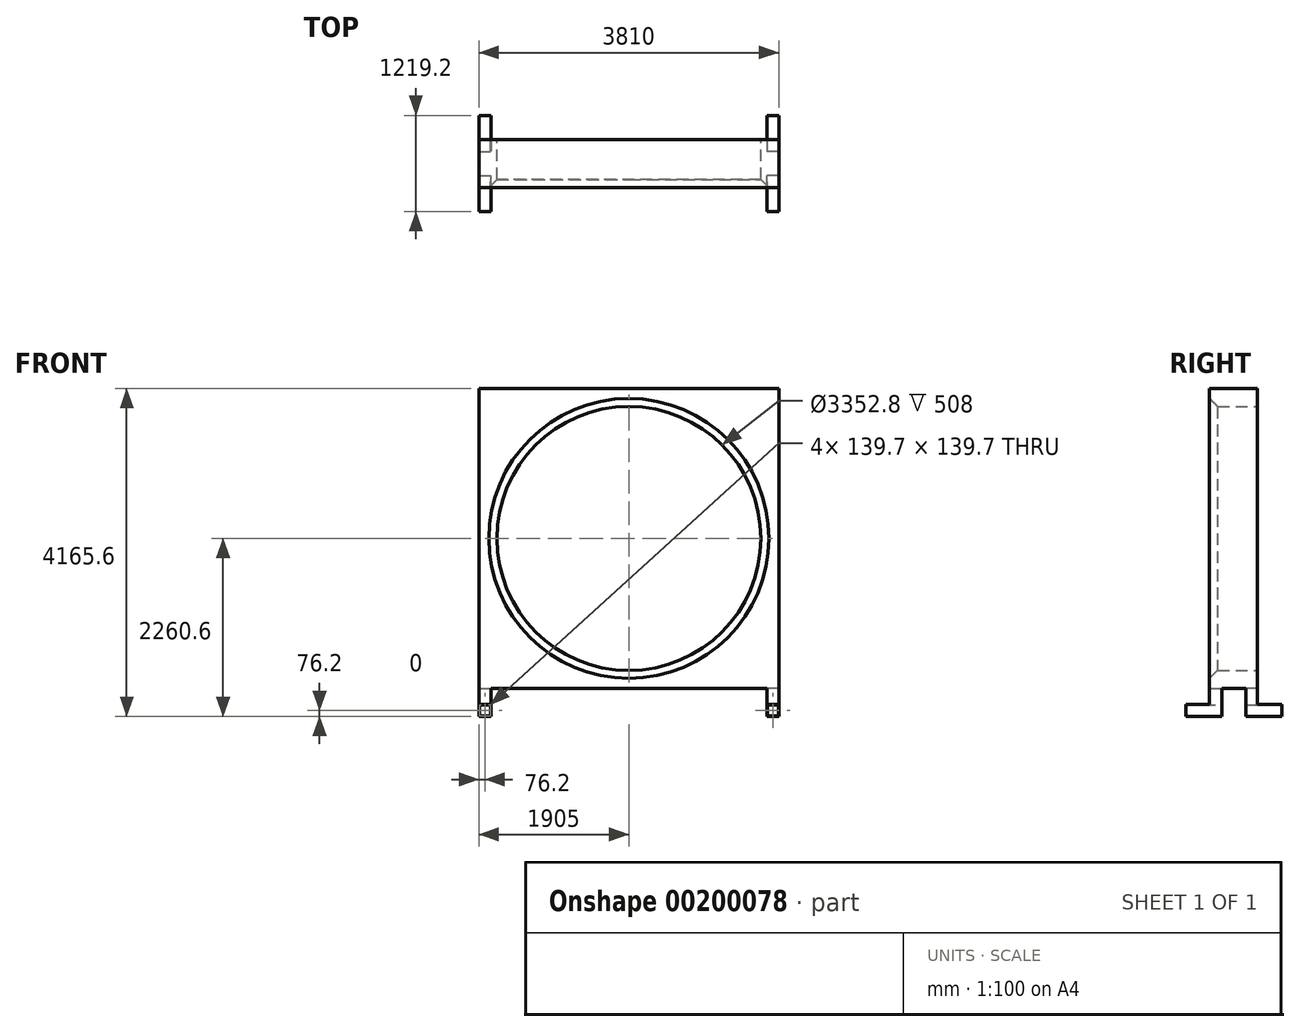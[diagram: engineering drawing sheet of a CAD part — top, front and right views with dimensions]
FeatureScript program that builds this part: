
annotation { "Feature Type Name" : "Feature", "Feature Type Description" : "" }
export const myFeature = defineFeature(function(context is Context, id is Id, definition is map)
    precondition{}
    {
        {
            var Q0;
            Q0=qCreatedBy(makeId("Front.planeOp"),FACE);
            var sketch = newSketch(context, id + "F0", { "sketchPlane" : qUnion([Q0])});
            skLineSegment(sketch, "E0.bottom", {"start": v(-1905, 1905) * mm, "end": v(1905, 1905) * mm});
            skLineSegment(sketch, "E0.top", {"start": v(-1905, -1905) * mm, "end": v(1905, -1905) * mm});
            skLineSegment(sketch, "E0.left", {"start": v(-1905, 1905) * mm, "end": v(-1905, -1905) * mm});
            skLineSegment(sketch, "E0.right", {"start": v(1905, 1905) * mm, "end": v(1905, -1905) * mm});
            skSolve(sketch);
        }
        {
            var Q0;
            Q0=makeQuery(id+"F0.imprint","IMPRINT",FACE,{"disambiguationData":[TD([[makeQuery(id+"F0.imprint","IMPRINT",EDGE,{"derivedFrom":sQuery(id+"F0.wireOp",EDGE,"E0.bottom")}),-1.0]])]});
            extrude(context, id + "F1", {"entities" : qUnion([Q0]), "depth" : 609.6 * mm});
        }
        {
            var Q0;
            Q0=makeQuery(id+"F1.opExtrude","CAP_FACE",FACE,{"disambiguationData":[OSD([sQuery(id+"F0.wireOp",EDGE,"E0.bottom"),sQuery(id+"F0.wireOp",EDGE,"E0.top"),sQuery(id+"F0.wireOp",EDGE,"E0.left"),sQuery(id+"F0.wireOp",EDGE,"E0.right")])],"isStart":false});
            var sketch = newSketch(context, id + "F2", { "sketchPlane" : qUnion([Q0])});
            skPoint(sketch, "E1", {"position": v(0, 0) * mm});
            skSolve(sketch);
        }
        {
            var Q0;
            Q0=sQuery(id+"F2.wireOp",VERTEX,"E1");
            var Q1;
            Q1=makeQuery(id+"F1.opExtrude","SWEPT_BODY",BODY,{"disambiguationData":[OSD([sQuery(id+"F0.wireOp",EDGE,"E0.bottom"),sQuery(id+"F0.wireOp",EDGE,"E0.top"),sQuery(id+"F0.wireOp",EDGE,"E0.left"),sQuery(id+"F0.wireOp",EDGE,"E0.right")])]});
            hole(context, id + "F3", {"style" : HoleStyle.C_SINK, "endStyle" : HoleEndStyle.THROUGH, "holeDiameter" : 3352.8 * mm, "cSinkDiameter" : 3556 * mm, "cSinkAngle" : 90 * degree, "locations" : qUnion([Q0]), "scope" : qUnion([Q1]), "isTappedThrough" : true});
        }
        {
            var Q0;
            Q0=makeQuery(id+"F1.opExtrude","SWEPT_FACE",FACE,{"disambiguationData":[OSD([sQuery(id+"F0.wireOp",EDGE,"E0.top")])]});
            var sketch = newSketch(context, id + "F4", { "sketchPlane" : qUnion([Q0])});
            skLineSegment(sketch, "E2.bottom", {"start": v(-1905, 609.6) * mm, "end": v(-1752.6, 609.6) * mm});
            skLineSegment(sketch, "E2.top", {"start": v(-1905, 457.2) * mm, "end": v(-1752.6, 457.2) * mm});
            skLineSegment(sketch, "E2.left", {"start": v(-1905, 609.6) * mm, "end": v(-1905, 457.2) * mm});
            skLineSegment(sketch, "E2.right", {"start": v(-1752.6, 609.6) * mm, "end": v(-1752.6, 457.2) * mm});
            skLineSegment(sketch, "E3.bottom", {"start": v(-1905, 0) * mm, "end": v(-1752.6, 0) * mm});
            skLineSegment(sketch, "E3.top", {"start": v(-1905, 152.4) * mm, "end": v(-1752.6, 152.4) * mm});
            skLineSegment(sketch, "E3.left", {"start": v(-1905, 0) * mm, "end": v(-1905, 152.4) * mm});
            skLineSegment(sketch, "E3.right", {"start": v(-1752.6, 0) * mm, "end": v(-1752.6, 152.4) * mm});
            skLineSegment(sketch, "E4.bottom", {"start": v(1905, 609.6) * mm, "end": v(1752.6, 609.6) * mm});
            skLineSegment(sketch, "E4.top", {"start": v(1905, 457.2) * mm, "end": v(1752.6, 457.2) * mm});
            skLineSegment(sketch, "E4.left", {"start": v(1905, 609.6) * mm, "end": v(1905, 457.2) * mm});
            skLineSegment(sketch, "E4.right", {"start": v(1752.6, 609.6) * mm, "end": v(1752.6, 457.2) * mm});
            skLineSegment(sketch, "E5.bottom", {"start": v(1905, 0) * mm, "end": v(1752.6, 0) * mm});
            skLineSegment(sketch, "E5.top", {"start": v(1905, 152.4) * mm, "end": v(1752.6, 152.4) * mm});
            skLineSegment(sketch, "E5.left", {"start": v(1905, 0) * mm, "end": v(1905, 152.4) * mm});
            skLineSegment(sketch, "E5.right", {"start": v(1752.6, 0) * mm, "end": v(1752.6, 152.4) * mm});
            skSolve(sketch);
        }
        {
            var Q0;
            Q0=makeQuery(id+"F4.imprint","IMPRINT",FACE,{"disambiguationData":[TD([[makeQuery(id+"F4.imprint","IMPRINT",EDGE,{"derivedFrom":sQuery(id+"F4.wireOp",EDGE,"E2.bottom")}),-1.0]])]});
            var Q1;
            Q1=makeQuery(id+"F4.imprint","IMPRINT",FACE,{"disambiguationData":[TD([[makeQuery(id+"F4.imprint","IMPRINT",EDGE,{"derivedFrom":sQuery(id+"F4.wireOp",EDGE,"E3.bottom")}),1.0]])]});
            var Q2;
            Q2=makeQuery(id+"F4.imprint","IMPRINT",FACE,{"disambiguationData":[TD([[makeQuery(id+"F4.imprint","IMPRINT",EDGE,{"derivedFrom":sQuery(id+"F4.wireOp",EDGE,"E5.bottom")}),1.0]])]});
            var Q3;
            Q3=makeQuery(id+"F4.imprint","IMPRINT",FACE,{"disambiguationData":[TD([[makeQuery(id+"F4.imprint","IMPRINT",EDGE,{"derivedFrom":sQuery(id+"F4.wireOp",EDGE,"E4.bottom")}),-1.0]])]});
            extrude(context, id + "F5", {"entities" : qUnion([Q0, Q1, Q2, Q3]), "operationType" : NewBodyOperationType.ADD, "depth" : 355.6 * mm});
        }
        {
            var Q0;
            Q0=makeQuery(id+"F5.boolean.opBoolean","MERGE",FACE,{"derivedFrom":[makeQuery(id+"F1.opExtrude","CAP_FACE",FACE,{"disambiguationData":[OSD([sQuery(id+"F0.wireOp",EDGE,"E0.bottom"),sQuery(id+"F0.wireOp",EDGE,"E0.top"),sQuery(id+"F0.wireOp",EDGE,"E0.left"),sQuery(id+"F0.wireOp",EDGE,"E0.right")])],"isStart":false}),makeQuery(id+"F5.opExtrude","SWEPT_FACE",FACE,{"disambiguationData":[OSD([sQuery(id+"F4.wireOp",EDGE,"E2.bottom")])]}),makeQuery(id+"F5.opExtrude","SWEPT_FACE",FACE,{"disambiguationData":[OSD([sQuery(id+"F4.wireOp",EDGE,"E4.bottom")])]})]});
            var sketch = newSketch(context, id + "F6", { "sketchPlane" : qUnion([Q0])});
            skLineSegment(sketch, "E6.bottom", {"start": v(-1905, -2260.6) * mm, "end": v(-1752.6, -2260.6) * mm});
            skLineSegment(sketch, "E6.top", {"start": v(-1905, -2108.2) * mm, "end": v(-1752.6, -2108.2) * mm});
            skLineSegment(sketch, "E6.left", {"start": v(-1905, -2260.6) * mm, "end": v(-1905, -2108.2) * mm});
            skLineSegment(sketch, "E6.right", {"start": v(-1752.6, -2260.6) * mm, "end": v(-1752.6, -2108.2) * mm});
            skLineSegment(sketch, "E7.bottom", {"start": v(1905, -2260.6) * mm, "end": v(1752.6, -2260.6) * mm});
            skLineSegment(sketch, "E7.top", {"start": v(1905, -2108.2) * mm, "end": v(1752.6, -2108.2) * mm});
            skLineSegment(sketch, "E7.left", {"start": v(1905, -2260.6) * mm, "end": v(1905, -2108.2) * mm});
            skLineSegment(sketch, "E7.right", {"start": v(1752.6, -2260.6) * mm, "end": v(1752.6, -2108.2) * mm});
            skSolve(sketch);
        }
        {
            var Q0;
            Q0=makeQuery(id+"F6.imprint","IMPRINT",FACE,{"disambiguationData":[TD([[makeQuery(id+"F6.imprint","IMPRINT",EDGE,{"derivedFrom":sQuery(id+"F6.wireOp",EDGE,"E6.bottom")}),1.0]])]});
            var Q1;
            Q1=makeQuery(id+"F6.imprint","IMPRINT",FACE,{"disambiguationData":[TD([[makeQuery(id+"F6.imprint","IMPRINT",EDGE,{"derivedFrom":sQuery(id+"F6.wireOp",EDGE,"E7.bottom")}),1.0]])]});
            extrude(context, id + "F7", {"entities" : qUnion([Q0, Q1]), "operationType" : NewBodyOperationType.ADD, "depth" : 304.8 * mm});
        }
        {
            var Q0;
            Q0=makeQuery(id+"F5.boolean.opBoolean","MERGE",FACE,{"derivedFrom":[makeQuery(id+"F1.opExtrude","CAP_FACE",FACE,{"disambiguationData":[OSD([sQuery(id+"F0.wireOp",EDGE,"E0.bottom"),sQuery(id+"F0.wireOp",EDGE,"E0.top"),sQuery(id+"F0.wireOp",EDGE,"E0.left"),sQuery(id+"F0.wireOp",EDGE,"E0.right")])],"isStart":true}),makeQuery(id+"F5.opExtrude","SWEPT_FACE",FACE,{"disambiguationData":[OSD([sQuery(id+"F4.wireOp",EDGE,"E3.bottom")])]}),makeQuery(id+"F5.opExtrude","SWEPT_FACE",FACE,{"disambiguationData":[OSD([sQuery(id+"F4.wireOp",EDGE,"E5.bottom")])]})]});
            var sketch = newSketch(context, id + "F8", { "sketchPlane" : qUnion([Q0])});
            skLineSegment(sketch, "E8.bottom", {"start": v(-1905, -2260.6) * mm, "end": v(-1752.6, -2260.6) * mm});
            skLineSegment(sketch, "E8.top", {"start": v(-1905, -2108.2) * mm, "end": v(-1752.6, -2108.2) * mm});
            skLineSegment(sketch, "E8.left", {"start": v(-1905, -2260.6) * mm, "end": v(-1905, -2108.2) * mm});
            skLineSegment(sketch, "E8.right", {"start": v(-1752.6, -2260.6) * mm, "end": v(-1752.6, -2108.2) * mm});
            skLineSegment(sketch, "E9.bottom", {"start": v(1905, -2260.6) * mm, "end": v(1752.6, -2260.6) * mm});
            skLineSegment(sketch, "E9.top", {"start": v(1905, -2108.2) * mm, "end": v(1752.6, -2108.2) * mm});
            skLineSegment(sketch, "E9.left", {"start": v(1905, -2260.6) * mm, "end": v(1905, -2108.2) * mm});
            skLineSegment(sketch, "E9.right", {"start": v(1752.6, -2260.6) * mm, "end": v(1752.6, -2108.2) * mm});
            skSolve(sketch);
        }
        {
            var Q0;
            Q0=makeQuery(id+"F8.imprint","IMPRINT",FACE,{"disambiguationData":[TD([[makeQuery(id+"F8.imprint","IMPRINT",EDGE,{"derivedFrom":sQuery(id+"F8.wireOp",EDGE,"E8.bottom")}),-1.0]])]});
            var Q1;
            Q1=makeQuery(id+"F8.imprint","IMPRINT",FACE,{"disambiguationData":[TD([[makeQuery(id+"F8.imprint","IMPRINT",EDGE,{"derivedFrom":sQuery(id+"F8.wireOp",EDGE,"E9.bottom")}),-1.0]])]});
            extrude(context, id + "F9", {"entities" : qUnion([Q0, Q1]), "operationType" : NewBodyOperationType.ADD, "depth" : 304.8 * mm});
        }
        {
            var Q0;
            Q0=makeQuery(id+"F5.opExtrude","SWEPT_FACE",FACE,{"disambiguationData":[OSD([sQuery(id+"F4.wireOp",EDGE,"E4.top")])]});
            var sketch = newSketch(context, id + "F10", { "sketchPlane" : qUnion([Q0])});
            skLineSegment(sketch, "E10.bottom", {"start": v(-1752.6, -2260.6) * mm, "end": v(-1905, -2260.6) * mm});
            skLineSegment(sketch, "E10.top", {"start": v(-1752.6, -2108.2) * mm, "end": v(-1905, -2108.2) * mm});
            skLineSegment(sketch, "E10.left", {"start": v(-1752.6, -2260.6) * mm, "end": v(-1752.6, -2108.2) * mm});
            skLineSegment(sketch, "E10.right", {"start": v(-1905, -2260.6) * mm, "end": v(-1905, -2108.2) * mm});
            skSolve(sketch);
        }
        {
            var Q0;
            Q0=makeQuery(id+"F9.opExtrude","CAP_FACE",FACE,{"disambiguationData":[OSD([sQuery(id+"F8.wireOp",EDGE,"E8.bottom"),sQuery(id+"F8.wireOp",EDGE,"E8.top"),sQuery(id+"F8.wireOp",EDGE,"E8.left"),sQuery(id+"F8.wireOp",EDGE,"E8.right")])],"isStart":false});
            var sketch = newSketch(context, id + "F11", { "sketchPlane" : qUnion([Q0])});
            skLineSegment(sketch, "E11.bottom", {"start": v(-1898.65, -2114.55) * mm, "end": v(-1758.95, -2114.55) * mm});
            skLineSegment(sketch, "E11.top", {"start": v(-1898.65, -2254.25) * mm, "end": v(-1758.95, -2254.25) * mm});
            skLineSegment(sketch, "E11.left", {"start": v(-1898.65, -2114.55) * mm, "end": v(-1898.65, -2254.25) * mm});
            skLineSegment(sketch, "E11.right", {"start": v(-1758.95, -2114.55) * mm, "end": v(-1758.95, -2254.25) * mm});
            skLineSegment(sketch, "E12.bottom", {"start": v(1758.95, -2114.55) * mm, "end": v(1898.65, -2114.55) * mm});
            skLineSegment(sketch, "E12.top", {"start": v(1758.95, -2254.25) * mm, "end": v(1898.65, -2254.25) * mm});
            skLineSegment(sketch, "E12.left", {"start": v(1758.95, -2114.55) * mm, "end": v(1758.95, -2254.25) * mm});
            skLineSegment(sketch, "E12.right", {"start": v(1898.65, -2114.55) * mm, "end": v(1898.65, -2254.25) * mm});
            skSolve(sketch);
        }
        {
            var Q0;
            Q0=makeQuery(id+"F11.imprint","IMPRINT",FACE,{"disambiguationData":[TD([[makeQuery(id+"F11.imprint","IMPRINT",EDGE,{"derivedFrom":sQuery(id+"F11.wireOp",EDGE,"E11.bottom")}),-1.0]])]});
            var Q1;
            Q1=makeQuery(id+"F11.imprint","IMPRINT",FACE,{"disambiguationData":[TD([[makeQuery(id+"F11.imprint","IMPRINT",EDGE,{"derivedFrom":sQuery(id+"F11.wireOp",EDGE,"E12.bottom")}),-1.0]])]});
            extrude(context, id + "F12", {"entities" : qUnion([Q0, Q1]), "operationType" : NewBodyOperationType.REMOVE, "oppositeDirection" : true, "depth" : 1270 * mm});
        }
    });
